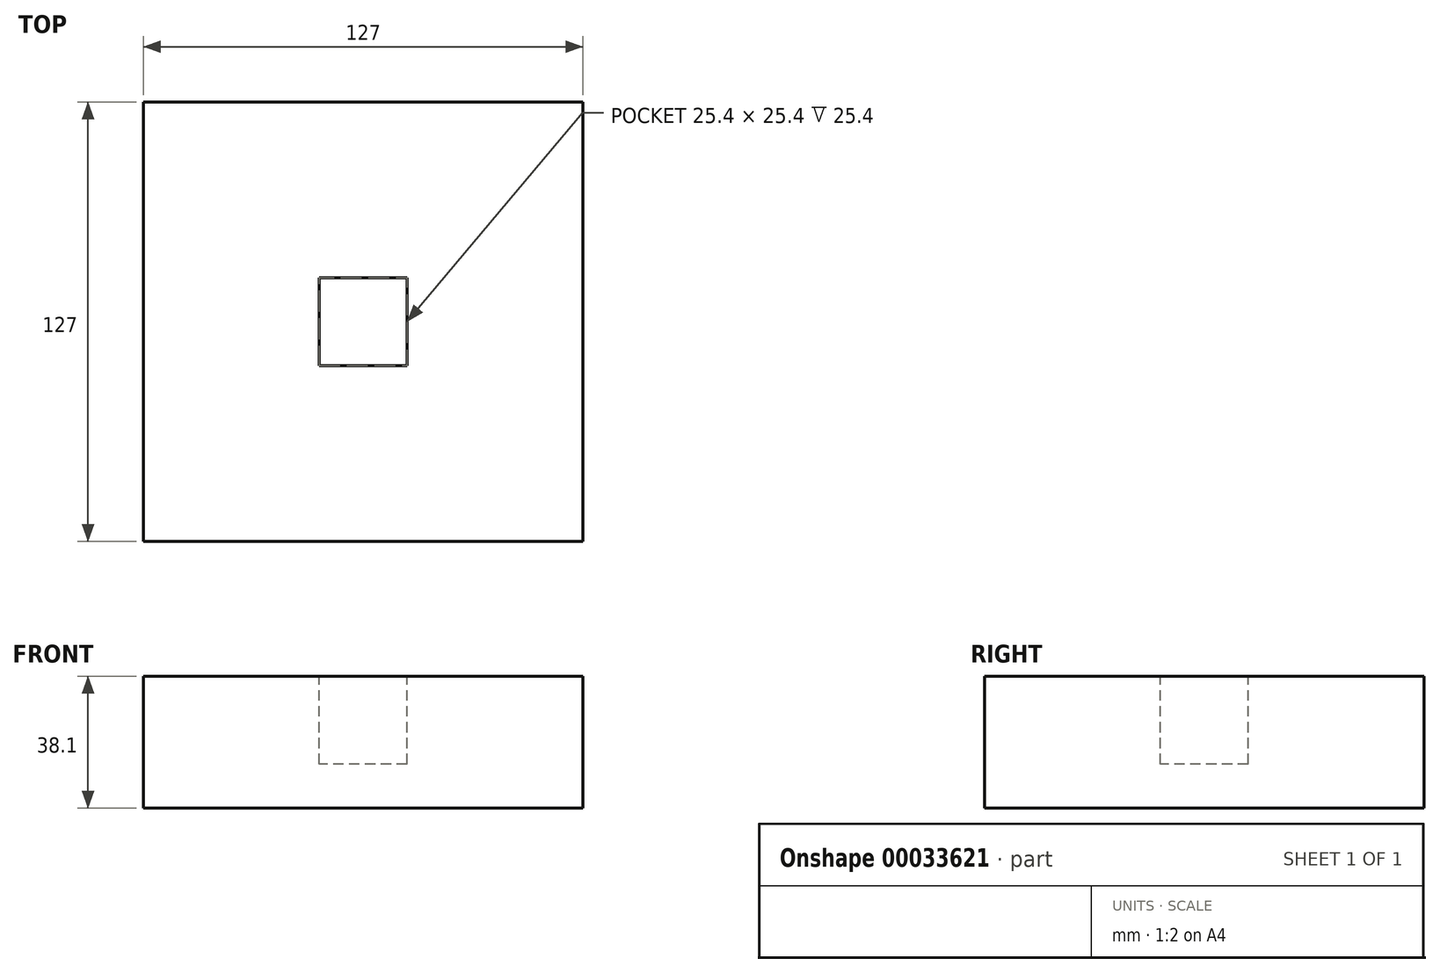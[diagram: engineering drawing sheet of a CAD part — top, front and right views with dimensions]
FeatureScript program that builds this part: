
annotation { "Feature Type Name" : "Feature", "Feature Type Description" : "" }
export const myFeature = defineFeature(function(context is Context, id is Id, definition is map)
    precondition{}
    {
        {
            var Q0;
            Q0=qCreatedBy(makeId("Front.planeOp"),FACE);
            var sketch = newSketch(context, id + "F0", { "sketchPlane" : qUnion([Q0])});
            skLineSegment(sketch, "E0.bottom", {"start": v(0, 0) * mm, "end": v(127, 0) * mm});
            skLineSegment(sketch, "E0.top", {"start": v(0, 38.1) * mm, "end": v(127, 38.1) * mm});
            skLineSegment(sketch, "E0.left", {"start": v(0, 0) * mm, "end": v(0, 38.1) * mm});
            skLineSegment(sketch, "E0.right", {"start": v(127, 0) * mm, "end": v(127, 38.1) * mm});
            skSolve(sketch);
        }
        {
            var Q0;
            Q0=makeQuery(id+"F0.imprint","IMPRINT",FACE,{"disambiguationData":[TD([[makeQuery(id+"F0.imprint","IMPRINT",EDGE,{"derivedFrom":sQuery(id+"F0.wireOp",EDGE,"E0.bottom")}),1.0]])]});
            extrude(context, id + "F1", {"entities" : qUnion([Q0]), "depth" : 127 * mm});
        }
        {
            var Q0;
            Q0=makeQuery(id+"F1.opExtrude","SWEPT_FACE",FACE,{"disambiguationData":[OSD([sQuery(id+"F0.wireOp",EDGE,"E0.top")])]});
            var sketch = newSketch(context, id + "F2", { "sketchPlane" : qUnion([Q0])});
            skLineSegment(sketch, "E1.bottom", {"start": v(76.2, -50.8) * mm, "end": v(50.8, -50.8) * mm});
            skLineSegment(sketch, "E1.top", {"start": v(76.2, -76.2) * mm, "end": v(50.8, -76.2) * mm});
            skLineSegment(sketch, "E1.left", {"start": v(76.2, -50.8) * mm, "end": v(76.2, -76.2) * mm});
            skLineSegment(sketch, "E1.right", {"start": v(50.8, -50.8) * mm, "end": v(50.8, -76.2) * mm});
            skSolve(sketch);
        }
        {
            var Q0;
            Q0=makeQuery(id+"F2.imprint","IMPRINT",FACE,{"disambiguationData":[TD([[makeQuery(id+"F2.imprint","IMPRINT",EDGE,{"derivedFrom":sQuery(id+"F2.wireOp",EDGE,"E1.bottom")}),1.0]])]});
            extrude(context, id + "F3", {"entities" : qUnion([Q0]), "operationType" : NewBodyOperationType.REMOVE, "oppositeDirection" : true, "depth" : 25.4 * mm});
        }
    });
